# Revit family: 31707-presto
name_source: partatom
category: Plumbing Fixtures
units: mm (PartAtom-declared; Revit-internal decimal feet)

## family parameters
Always vertical = Yes
Cut with Voids When Loaded = No
Maintain Annotation Orientation = No
OmniClass Number = 23.45.00.00
OmniClass Title = Sanitary, Laundry, and Cleaning Equipment
Part Type = Normal
Room Calculation Point = No
Round Connector Dimension = Use Diameter
Shared = No
Work Plane-Based = Yes

## types (1)
- 31707- Les Robinets PRESTO
    Default Elevation = 1219 mm
    Description = PRESTO 12 NEO
    Model = 31707
    Recommended pressure = 3.0 bar
    URL = https://www.prestodatashare.com
    brand = Les Robinets PRESTO
    flow = 6.0 L/min
    flow time = 6.0 s
    material = Default
    min flow = 2.0 L/min
    min pressure = 1.0 bar
    pressure = 5.0 bar
    range = PRESTO 12 NEO
    ref = 31707 - Wall-mounted exposed timed-flow urinal tap, rear water inlet, without nut

## geometry (parser evidence)
native form markers: Sweep x3
no freeform markers — native parametric forms only
